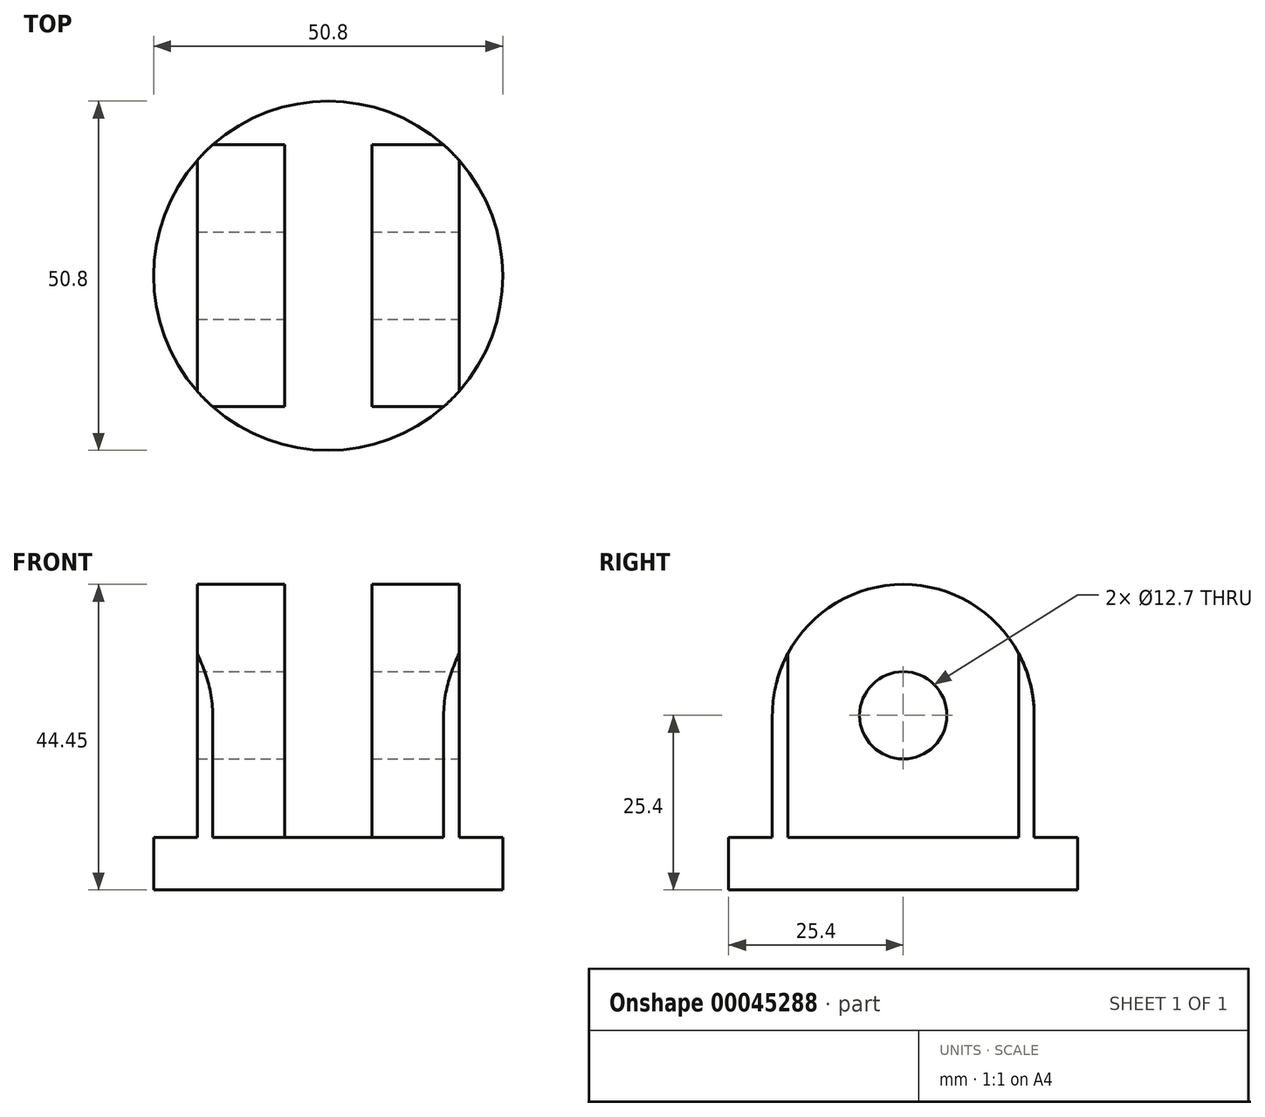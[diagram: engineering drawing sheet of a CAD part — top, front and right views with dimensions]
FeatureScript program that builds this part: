
annotation { "Feature Type Name" : "Feature", "Feature Type Description" : "" }
export const myFeature = defineFeature(function(context is Context, id is Id, definition is map)
    precondition{}
    {
        {
            var Q0;
            Q0=qCreatedBy(makeId("Top.planeOp"),FACE);
            var sketch = newSketch(context, id + "F0", { "sketchPlane" : qUnion([Q0])});
            skCircle(sketch, "E0", {"center": v(0, 0) * mm, "radius": 25.4 * mm});
            skSolve(sketch);
        }
        {
            var Q0;
            Q0 = qSketchRegion(id + "F0", true);
            extrude(context, id + "F1", {"entities" : qUnion([Q0]), "endBound" : BoundingType.SYMMETRIC, "depth" : 50.8 * mm});
        }
        {
            var Q0;
            Q0=makeQuery(id+"F1.opExtrude","CAP_FACE",FACE,{"disambiguationData":[OSD([sQuery(id+"F0.wireOp",EDGE,"E0")])],"isStart":false});
            var sketch = newSketch(context, id + "F2", { "sketchPlane" : qUnion([Q0])});
            skLineSegment(sketch, "E1.left", {"start": v(-6.35, 38.1) * mm, "end": v(-6.35, -38.1) * mm});
            skLineSegment(sketch, "E1.right", {"start": v(6.35, 38.1) * mm, "end": v(6.35, -38.21) * mm});
            skLineSegment(sketch, "E2.right", {"start": v(-12.7, 38.1) * mm, "end": v(-12.7, -38.1) * mm, "construction": true});
            skLineSegment(sketch, "E3.left", {"start": v(12.7, 38.1) * mm, "end": v(12.7, -38.1) * mm, "construction": true});
            skLineSegment(sketch, "E4.trimOffspring", {"start": v(-6.35, 38.1) * mm, "end": v(6.35, 38.1) * mm});
            skLineSegment(sketch, "E5.trimOffspring", {"start": v(-6.35, -38.1) * mm, "end": v(6.35, -38.1) * mm});
            skLineSegment(sketch, "E6.1.0.0", {"start": v(19.05, 38.1) * mm, "end": v(19.05, -38.1) * mm});
            skLineSegment(sketch, "E6.1.0.1", {"start": v(19.05, -38.1) * mm, "end": v(31.75, -38.1) * mm});
            skLineSegment(sketch, "E6.1.0.2", {"start": v(19.05, 38.1) * mm, "end": v(31.75, 38.1) * mm});
            skLineSegment(sketch, "E6.1.0.3", {"start": v(31.75, 38.1) * mm, "end": v(31.75, -38.21) * mm});
            skLineSegment(sketch, "E6.direction1", {"start": v(-6.35, -38.1) * mm, "end": v(19.05, -38.1) * mm, "construction": true});
            skLineSegment(sketch, "E7.1.0.0", {"start": v(-31.75, 38.1) * mm, "end": v(-31.75, -38.1) * mm});
            skLineSegment(sketch, "E7.1.0.1", {"start": v(-19.05, 38.1) * mm, "end": v(-19.05, -38.21) * mm});
            skLineSegment(sketch, "E7.1.0.2", {"start": v(-31.75, 38.1) * mm, "end": v(-19.05, 38.1) * mm});
            skLineSegment(sketch, "E7.1.0.3", {"start": v(-31.75, -38.1) * mm, "end": v(-19.05, -38.1) * mm});
            skLineSegment(sketch, "E7.direction1", {"start": v(6.35, -38.1) * mm, "end": v(-19.05, -38.1) * mm, "construction": true});
            skSolve(sketch);
        }
        {
            var Q0;
            Q0 = qSketchRegion(id + "F2", true);
            extrude(context, id + "F3", {"entities" : qUnion([Q0]), "operationType" : NewBodyOperationType.REMOVE, "oppositeDirection" : true, "depth" : 43.18 * mm});
        }
        {
            var Q0;
            Q0=qCreatedBy(makeId("Right.planeOp"),FACE);
            var sketch = newSketch(context, id + "F4", { "sketchPlane" : qUnion([Q0])});
            skCircle(sketch, "E8", {"center": v(0, 0) * mm, "radius": 6.35 * mm});
            skArc(sketch, "E9.0", {"start": v(19.05, 0) * mm, "mid": v(0, 19.05) * mm, "end": v(-19.05, 0) * mm});
            skLineSegment(sketch, "E10.bottom", {"start": v(38.1, 38.1) * mm, "end": v(-38.1, 38.1) * mm});
            skLineSegment(sketch, "E10.top", {"start": v(38.1, 0) * mm, "end": v(19.05, 0) * mm});
            skLineSegment(sketch, "E10.left", {"start": v(38.1, 38.1) * mm, "end": v(38.1, -17.78) * mm});
            skLineSegment(sketch, "E10.right", {"start": v(-38.1, 38.1) * mm, "end": v(-38.1, -17.78) * mm});
            skLineSegment(sketch, "E11", {"start": v(0, 0) * mm, "end": v(0, 66.23) * mm, "construction": true});
            skLineSegment(sketch, "E12.trimOffspring", {"start": v(-19.05, 0) * mm, "end": v(-38.1, 0) * mm});
            skLineSegment(sketch, "E13.0", {"start": v(38.1, -17.78) * mm, "end": v(19.05, -17.78) * mm});
            skLineSegment(sketch, "E14", {"start": v(-19.05, 0) * mm, "end": v(-19.05, -17.78) * mm});
            skLineSegment(sketch, "E15", {"start": v(19.05, 0) * mm, "end": v(19.05, -17.78) * mm});
            skLineSegment(sketch, "E16.trimOffspring", {"start": v(-19.05, -17.78) * mm, "end": v(-38.1, -17.78) * mm});
            skSolve(sketch);
        }
        {
            var Q0;
            Q0 = qSketchRegion(id + "F4", true);
            extrude(context, id + "F5", {"entities" : qUnion([Q0]), "operationType" : NewBodyOperationType.REMOVE, "endBound" : BoundingType.SYMMETRIC, "oppositeDirection" : true, "depth" : 50.8 * mm});
        }
    });
